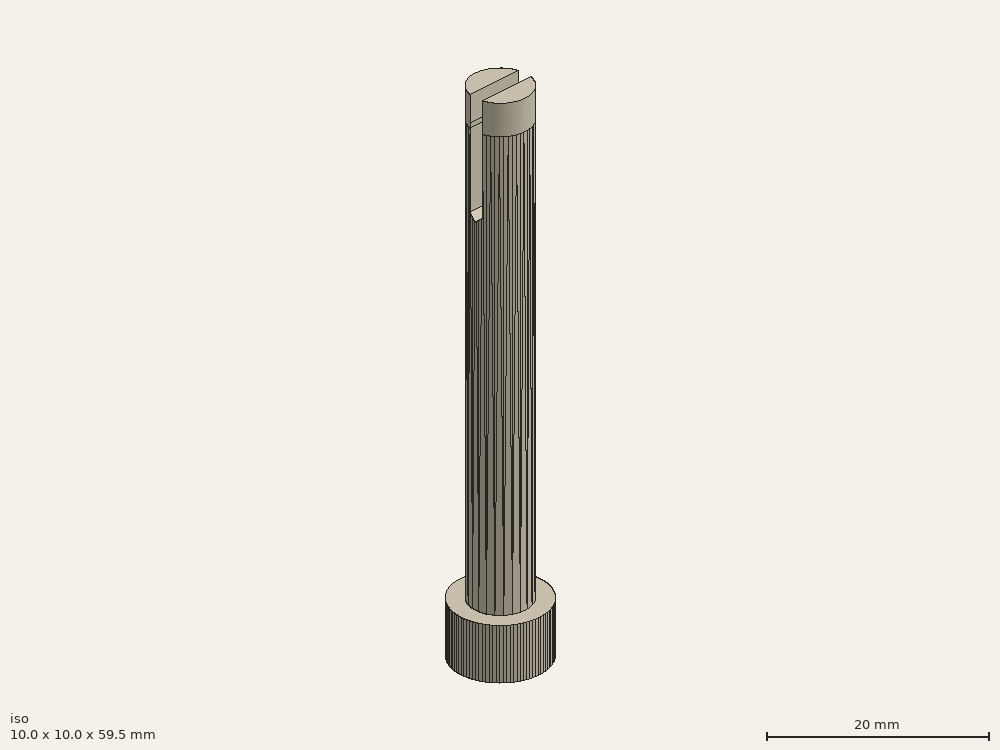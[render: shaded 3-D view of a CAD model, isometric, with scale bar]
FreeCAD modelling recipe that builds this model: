
FCSTD DOCUMENT  (FreeCAD 0.17R13522 (Git))
Label: v6_bastago_largo
License: CreativeCommons Attribution-ShareAlike
LicenseURL: http://creativecommons.org/licenses/by-sa/4.0/
objects: Part::Cut×3, Part::Box×2, Part::Feature×1, Part::Cylinder×1, Part::Fuse×1, Part::Chamfer×1
note: 9 computed .brp shape members not serialized (recipe doc carries the construction recipe); baked Part::Feature solids carry a one-line shape summary decoded from their .brp

FEATURE [Part::Feature] bastago_largo001_solid001  label="bastago_largo001 (Solid)001"
  shape: bbox 10 x 9.995 x 58.5 mm, 275 faces (baked)
FEATURE [Part::Box] Box  label="Cube"
  AttacherType = Attacher::AttachEngine3D
  Height = 10
  Length = 15
  Placement = pos=(-7,-8,-8) rot=(0,0,1;0rad)
  Width = 15
FEATURE [Part::Cut] Cut
  Base = -> bastago_largo001_solid001
  Refine = true
  Tool = -> Box
FEATURE [Part::Box] Box001  label="Cube001"
  AttacherType = Attacher::AttachEngine3D
  Height = 16
  Length = 10
  Placement = pos=(-5,-0.8,48.5) rot=(0,0,1;0rad)
  Width = 1.6
FEATURE [Part::Cut] Cut001  label="bastago con encastres"
  Base = -> Cut
  Refine = true
  Tool = -> Box001
FEATURE [Part::Cylinder] Cylinder
  Angle = 360
  AttacherType = Attacher::AttachEngine3D
  Height = 3.5
  Placement = pos=(0,0,58) rot=(0,0,1;0rad)
  Radius = 3.2
FEATURE [Part::Cut] Cut002
  Base = -> Cylinder
  Refine = true
  Tool = -> Box001
FEATURE [Part::Fuse] Fusion
  Base = -> Cut001
  Refine = true
  Tool = -> Cut002
FEATURE [Part::Chamfer] Chamfer
  Base = -> Fusion
  Edges = 2 edges r=0.7: [Edge534,Edge538]
